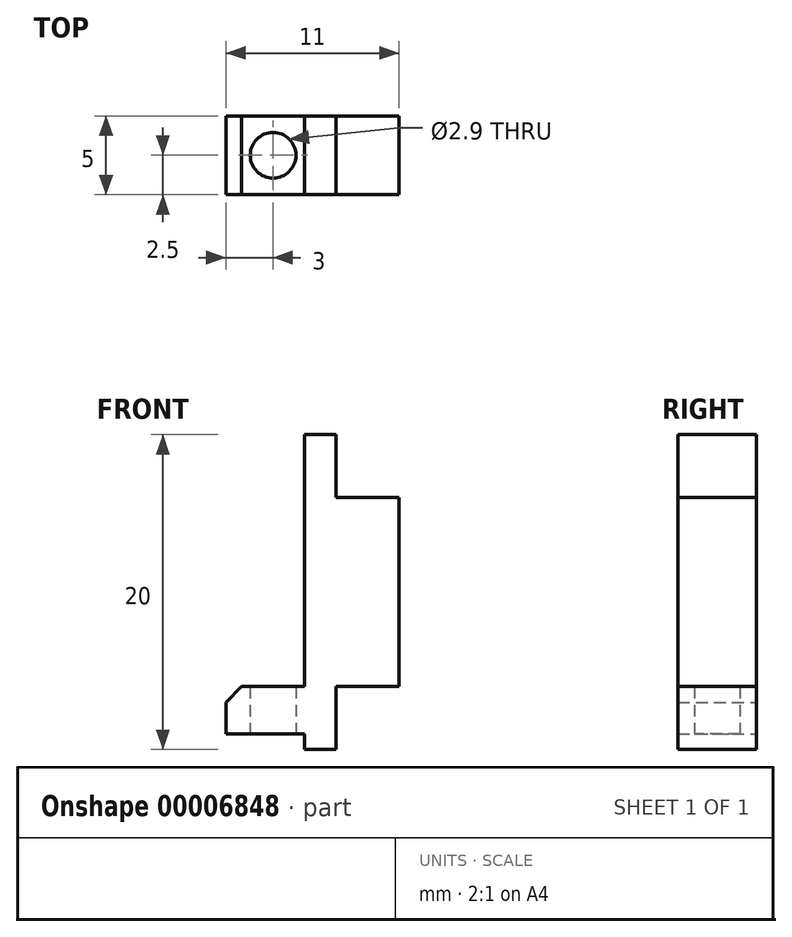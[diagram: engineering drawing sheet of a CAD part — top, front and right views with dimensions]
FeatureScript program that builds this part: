
annotation { "Feature Type Name" : "Feature", "Feature Type Description" : "" }
export const myFeature = defineFeature(function(context is Context, id is Id, definition is map)
    precondition{}
    {
        {
            var Q0;
            Q0=qCreatedBy(makeId("Front.planeOp"),FACE);
            var sketch = newSketch(context, id + "F0", { "sketchPlane" : qUnion([Q0])});
            skLineSegment(sketch, "E0", {"start": v(0, 0) * mm, "end": v(0, 1) * mm});
            skLineSegment(sketch, "E1", {"start": v(0, 20) * mm, "end": v(2, 20) * mm});
            skLineSegment(sketch, "E2", {"start": v(2, 20) * mm, "end": v(2, 16) * mm});
            skLineSegment(sketch, "E3", {"start": v(2, 16) * mm, "end": v(6, 16) * mm});
            skLineSegment(sketch, "E4", {"start": v(6, 16) * mm, "end": v(6, 4) * mm});
            skLineSegment(sketch, "E5", {"start": v(6, 4) * mm, "end": v(2, 4) * mm});
            skLineSegment(sketch, "E6", {"start": v(2, 4) * mm, "end": v(2, 0) * mm});
            skLineSegment(sketch, "E7", {"start": v(2, 0) * mm, "end": v(0, 0) * mm});
            skLineSegment(sketch, "E8", {"start": v(-5, 1) * mm, "end": v(0, 1) * mm});
            skLineSegment(sketch, "E9.trimOffspring", {"start": v(0, 4) * mm, "end": v(0, 20) * mm});
            skLineSegment(sketch, "E10", {"start": v(0, 4) * mm, "end": v(-4, 4) * mm});
            skLineSegment(sketch, "E11", {"start": v(-4, 4) * mm, "end": v(-5, 3) * mm});
            skLineSegment(sketch, "E12", {"start": v(-5, 3) * mm, "end": v(-5, 1) * mm});
            skSolve(sketch);
        }
        {
            var Q0;
            Q0=makeQuery(id+"F0.imprint","IMPRINT",FACE,{"disambiguationData":[TD([[makeQuery(id+"F0.imprint","IMPRINT",EDGE,{"derivedFrom":sQuery(id+"F0.wireOp",EDGE,"E0")}),-1.0]])]});
            extrude(context, id + "F1", {"entities" : qUnion([Q0]), "depth" : 5 * mm});
        }
        {
            var Q0;
            Q0=makeQuery(id+"F1.opExtrude","SWEPT_FACE",FACE,{"disambiguationData":[OSD([sQuery(id+"F0.wireOp",EDGE,"E8")])]});
            var sketch = newSketch(context, id + "F2", { "sketchPlane" : qUnion([Q0])});
            skCircle(sketch, "E13", {"center": v(-2, 2.5) * mm, "radius": 1.45 * mm});
            skLineSegment(sketch, "E14", {"start": v(-5, 2.5) * mm, "end": v(0, 2.5) * mm, "construction": true});
            skSolve(sketch);
        }
        {
            var Q0;
            Q0 = qSketchRegion(id + "F2", true);
            extrude(context, id + "F3", {"entities" : qUnion([Q0]), "operationType" : NewBodyOperationType.REMOVE, "endBound" : BoundingType.UP_TO_NEXT, "oppositeDirection" : true, "depth" : 25 * mm});
        }
    });
